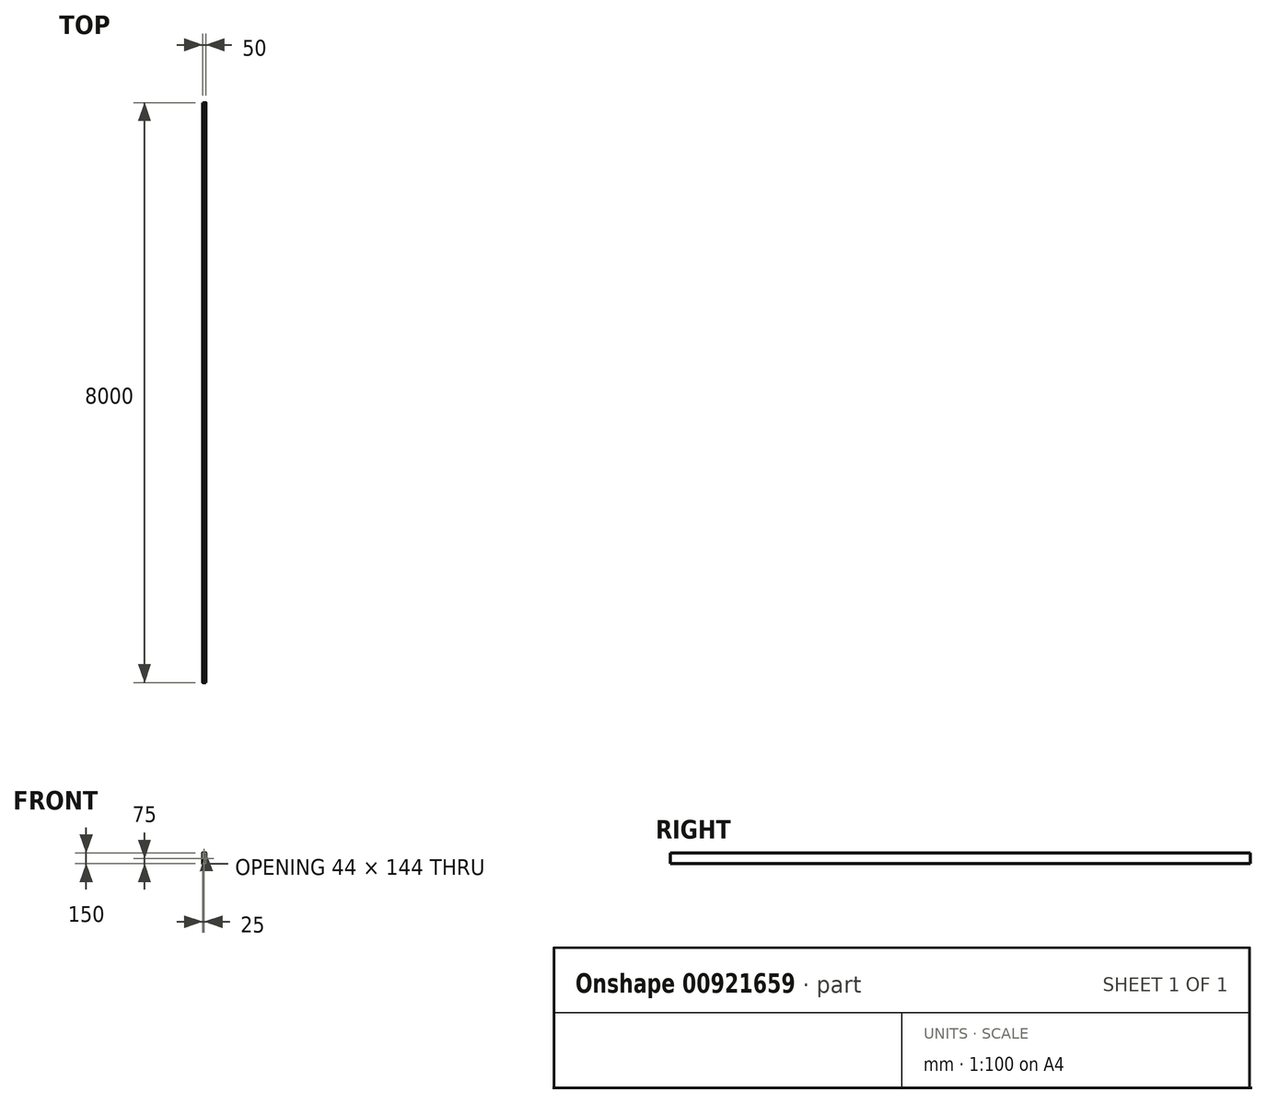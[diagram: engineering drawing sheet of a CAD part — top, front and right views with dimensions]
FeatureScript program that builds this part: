
annotation { "Feature Type Name" : "Feature", "Feature Type Description" : "" }
export const myFeature = defineFeature(function(context is Context, id is Id, definition is map)
    precondition{}
    {
        {
            var Q0;
            Q0=qCreatedBy(makeId("Front.planeOp"),FACE);
            var sketch = newSketch(context, id + "F0", { "sketchPlane" : qUnion([Q0])});
            skLineSegment(sketch, "E0.bottom", {"start": v(2.4, 0) * mm, "end": v(47.6, 0) * mm});
            skLineSegment(sketch, "E0.top", {"start": v(2.4, 150) * mm, "end": v(47.6, 150) * mm});
            skLineSegment(sketch, "E0.left", {"start": v(0, 2.4) * mm, "end": v(0, 147.6) * mm});
            skLineSegment(sketch, "E0.right", {"start": v(50, 2.4) * mm, "end": v(50, 147.6) * mm});
            skPoint(sketch, "E1.visualSharp", {"position": v(0, 150) * mm});
            skArc(sketch, "E1.filletArc", {"start": v(2.4, 150) * mm, "mid": v(0.7, 149.3) * mm, "end": v(0, 147.6) * mm});
            skPoint(sketch, "E2.visualSharp", {"position": v(50, 150) * mm});
            skArc(sketch, "E2.filletArc", {"start": v(50, 147.6) * mm, "mid": v(49.3, 149.3) * mm, "end": v(47.6, 150) * mm});
            skPoint(sketch, "E3.visualSharp", {"position": v(0, 0) * mm});
            skArc(sketch, "E3.filletArc", {"start": v(0, 2.4) * mm, "mid": v(0.7, 0.7) * mm, "end": v(2.4, 0) * mm});
            skPoint(sketch, "E4.visualSharp", {"position": v(50, 0) * mm});
            skArc(sketch, "E4.filletArc", {"start": v(47.6, 0) * mm, "mid": v(49.3, 0.7) * mm, "end": v(50, 2.4) * mm});
            skLineSegment(sketch, "E5.0", {"start": v(3, 5.4) * mm, "end": v(3, 144.6) * mm});
            skLineSegment(sketch, "E6.0", {"start": v(5.4, 147) * mm, "end": v(44.6, 147) * mm});
            skLineSegment(sketch, "E7.0", {"start": v(47, 5.4) * mm, "end": v(47, 144.6) * mm});
            skLineSegment(sketch, "E8.0", {"start": v(5.4, 3) * mm, "end": v(44.6, 3) * mm});
            skArc(sketch, "E9.filletArc", {"start": v(5.4, 147) * mm, "mid": v(3.7, 146.3) * mm, "end": v(3, 144.6) * mm});
            skArc(sketch, "E10.filletArc", {"start": v(3, 5.4) * mm, "mid": v(3.7, 3.7) * mm, "end": v(5.4, 3) * mm});
            skArc(sketch, "E11.filletArc", {"start": v(47, 144.6) * mm, "mid": v(46.3, 146.3) * mm, "end": v(44.6, 147) * mm});
            skArc(sketch, "E12.filletArc", {"start": v(44.6, 3) * mm, "mid": v(46.3, 3.7) * mm, "end": v(47, 5.4) * mm});
            skSolve(sketch);
        }
        {
            var Q0;
            Q0=qSketchRegion(id+"F0",true);
            extrude(context, id + "F1", {"entities" : qUnion([Q0]), "depth" : 8000 * mm, "offsetDistance" : 25 * mm});
        }
    });
